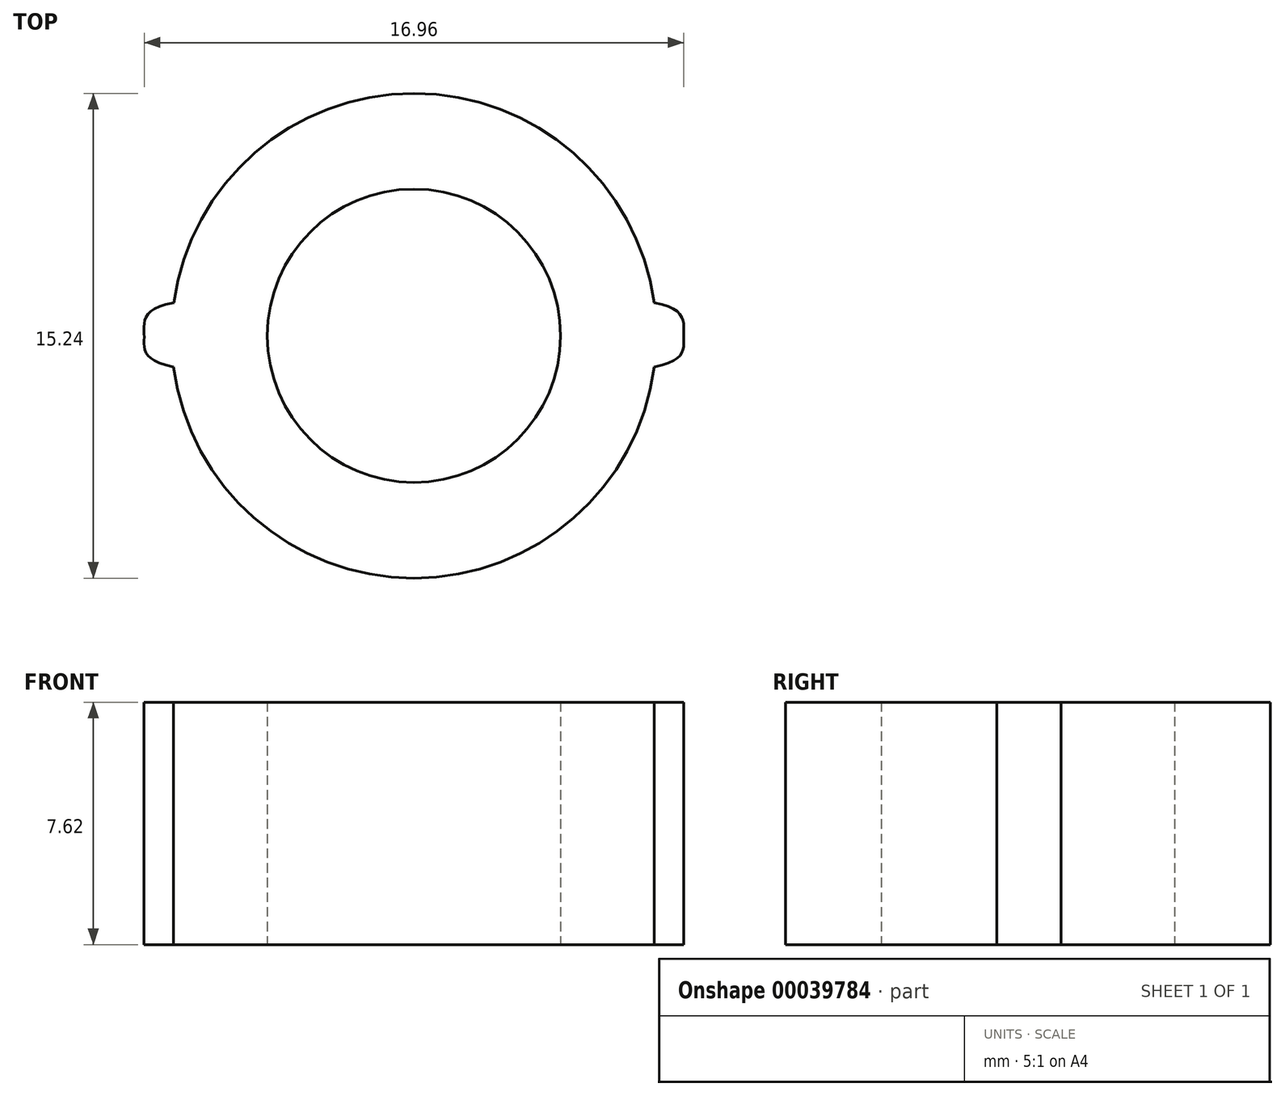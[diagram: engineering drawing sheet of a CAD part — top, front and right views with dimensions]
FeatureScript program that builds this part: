
annotation { "Feature Type Name" : "Feature", "Feature Type Description" : "" }
export const myFeature = defineFeature(function(context is Context, id is Id, definition is map)
    precondition{}
    {
        {
            var Q0;
            Q0=qCreatedBy(makeId("Top.planeOp"),FACE);
            var sketch = newSketch(context, id + "F0", { "sketchPlane" : qUnion([Q0])});
            skCircle(sketch, "E0", {"center": v(0, 0) * mm, "radius": 7.62 * mm});
            skLineSegment(sketch, "E1", {"start": v(-7.62, 0) * mm, "end": v(7.62, 0) * mm, "construction": true});
            skCircle(sketch, "E2", {"center": v(0, 0) * mm, "radius": 4.61 * mm});
            skLineSegment(sketch, "E3", {"start": v(0, 4.61) * mm, "end": v(0, -4.61) * mm, "construction": true});
            skFitSpline(sketch, "E4", {"points": [v(-7.55, 1.04) * mm, v(-8.48, 0) * mm, v(-7.56, -0.98) * mm], "startDerivative": vector(-6.24, -1.1) * mm, "endDerivative": vector(6.24, -1.28) * mm});
            skLineSegment(sketch, "E5", {"start": v(-7.62, 0) * mm, "end": v(-8.48, 0) * mm, "construction": true});
            skLineSegment(sketch, "E6", {"start": v(-7.62, 0) * mm, "end": v(-7.62, -0.98) * mm, "construction": true});
            skLineSegment(sketch, "E7", {"start": v(0, 7.62) * mm, "end": v(-0.98, 7.62) * mm, "construction": true});
            skLineSegment(sketch, "E8", {"start": v(0, 7.62) * mm, "end": v(1, 7.62) * mm, "construction": true});
            skFitSpline(sketch, "E9.MirrorCS", {"points": [v(7.55, 1.04) * mm, v(8.48, 0) * mm, v(7.56, -0.98) * mm], "startDerivative": vector(6.24, -1.1) * mm, "endDerivative": vector(-6.24, -1.28) * mm});
            skSolve(sketch);
        }
        {
            var Q0;
            Q0 = qSketchRegion(id + "F0", true);
            extrude(context, id + "F1", {"entities" : qUnion([Q0]), "depth" : 7.62 * mm});
        }
    });
